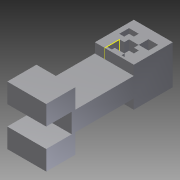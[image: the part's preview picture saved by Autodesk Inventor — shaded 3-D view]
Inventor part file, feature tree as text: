
AUTODESK INVENTOR PART (.ipt)
format: ipt  version: 2012 (Build 160160000, 160)  size: 197,120 bytes
history: native  units: in
note: dims shown in document units (in); Inventor stores cm internally (conversion verified against a paired STEP export)
features: sketch x14, extrude x13
ambient origin geometry x8: Origin, YZ Plane, XZ Plane, XY Plane, X Axis, Y Axis, Z Axis, Center Point
bodies: Solid1 (feature_tree)
feature tree (27):
  extrude  "Extrusion1"  Depth=2.0in
  extrude  "Extrusion2"  Depth=2.0in TaperAngle=0.0deg
  extrude  "Extrusion3"  Depth=6.0in TaperAngle=0.0deg
  extrude  "Extrusion4"  Depth=4.0in
  extrude  "Extrusion5"  Depth=1.0in
  extrude  "Extrusion6"  Depth=1.0in
  extrude  "Extrusion7"  Depth=1.0in TaperAngle=0.0deg
  extrude  "Extrusion8"  Depth=1.5in
  sketch  "Sketch9"  dims[d22=1.0in d23=0.0in d24=1.0in]
  extrude  "Extrusion9"  Depth=1.0in
  extrude  "Extrusion10"  Depth=1.0in TaperAngle=0.0deg
  extrude  "Extrusion11"  Depth=0.5in TaperAngle=0.0deg
  extrude  "Extrusion12"  Depth=0.2in TaperAngle=0.0deg
  extrude  "Extrusion13"  [1 undecoded]
  sketch  "Sketch1"  dims[d0=4.0in d1=2.0in]
  sketch  "Sketch2"  dims[d2=3.0in d3=0.0in d4=2.0in d5=0.0in]
  sketch  "Sketch3"  dims[d6=3.0in d7=0.0in d8=6.0in d9=0.0in]
  sketch  "Sketch4"  dims[d10=4.0in d11=4.0in]
  sketch  "Sketch5"  dims[d12=4.0in d13=0.0in d14=1.0in]
  sketch  "Sketch6"  dims[d15=1.0in d16=1.0in]
  sketch  "Sketch7"  dims[d17=1.0in d18=1.0in d19=0.0in]
  sketch  "Sketch8"  dims[d20=1.5in d21=1.5in]
  sketch  "Sketch10"  dims[d25=1.0in d26=0.0in d27=1.0in d28=0.0in]
  sketch  "Sketch11"  dims[d29=0.5in d30=0.0in d31=0.5in d32=0.0in]
  sketch  "Sketch12"  dims[d33=0.2in d34=0.0in d35=0.2in d36=0.0in]
  sketch  "Sketch13"
  sketch  "Sketch14"
note: 1 required parameter value undecoded (feature->parameter linkage not recoverable at this tier; creation-order binding heuristic only, values carry confidence <= 0.55)
